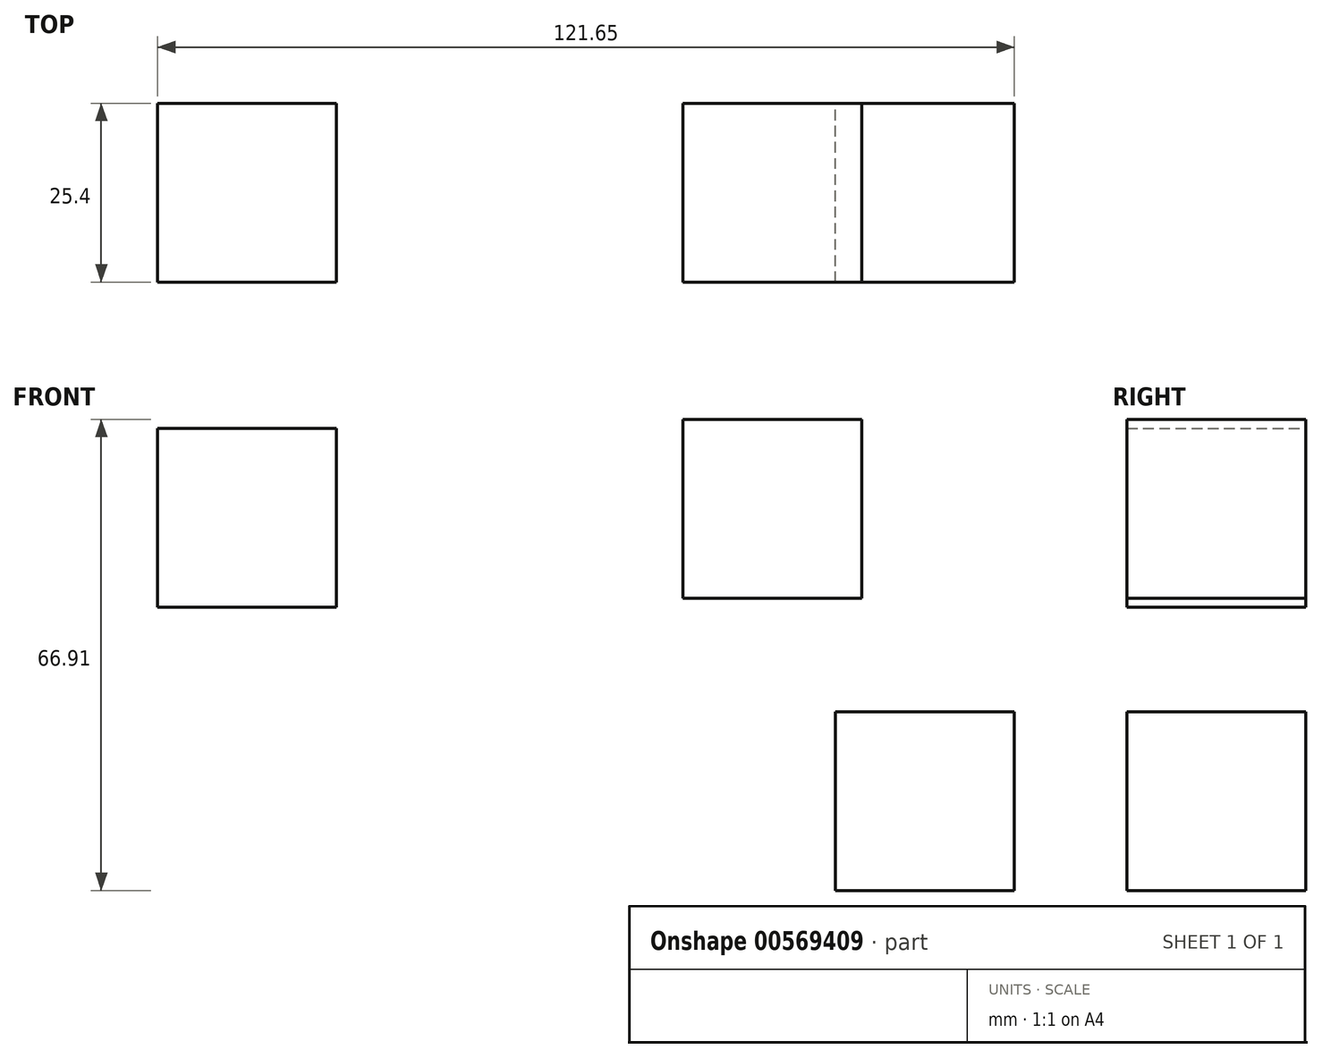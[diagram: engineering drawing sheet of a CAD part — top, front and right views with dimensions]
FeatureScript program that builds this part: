
annotation { "Feature Type Name" : "Feature", "Feature Type Description" : "" }
export const myFeature = defineFeature(function(context is Context, id is Id, definition is map)
    precondition{}
    {
        {
            var Q0;
            Q0=qCreatedBy(makeId("Front.planeOp"),FACE);
            var sketch = newSketch(context, id + "F0", { "sketchPlane" : qUnion([Q0])});
            skLineSegment(sketch, "E0.bottom", {"start": v(-67.13, 65.63) * mm, "end": v(-41.73, 65.63) * mm});
            skLineSegment(sketch, "E0.top", {"start": v(-67.13, 40.23) * mm, "end": v(-41.73, 40.23) * mm});
            skLineSegment(sketch, "E0.left", {"start": v(-67.13, 65.63) * mm, "end": v(-67.13, 40.23) * mm});
            skLineSegment(sketch, "E0.right", {"start": v(-41.73, 65.63) * mm, "end": v(-41.73, 40.23) * mm});
            skSolve(sketch);
        }
        {
            var Q0;
            Q0 = qSketchRegion(id + "F0", true);
            extrude(context, id + "F1", {"entities" : qUnion([Q0]), "depth" : 25.4 * mm, "offsetDistance" : 25.4 * mm});
        }
        {
            var Q0;
            Q0=qCreatedBy(makeId("Front.planeOp"),FACE);
            var sketch = newSketch(context, id + "F2", { "sketchPlane" : qUnion([Q0])});
            skLineSegment(sketch, "E1.bottom", {"start": v(7.48, 66.9) * mm, "end": v(32.88, 66.9) * mm});
            skLineSegment(sketch, "E1.top", {"start": v(7.48, 41.5) * mm, "end": v(32.88, 41.5) * mm});
            skLineSegment(sketch, "E1.left", {"start": v(7.48, 66.9) * mm, "end": v(7.48, 41.5) * mm});
            skLineSegment(sketch, "E1.right", {"start": v(32.88, 66.9) * mm, "end": v(32.88, 41.5) * mm});
            skSolve(sketch);
        }
        {
            var Q0;
            Q0 = qSketchRegion(id + "F2", true);
            extrude(context, id + "F3", {"entities" : qUnion([Q0]), "depth" : 25.4 * mm, "offsetDistance" : 25.4 * mm});
        }
        {
            var Q0;
            Q0=qCreatedBy(makeId("Front.planeOp"),FACE);
            var sketch = newSketch(context, id + "F4", { "sketchPlane" : qUnion([Q0])});
            skLineSegment(sketch, "E2.bottom", {"start": v(54.52, 25.4) * mm, "end": v(29.12, 25.4) * mm});
            skLineSegment(sketch, "E2.top", {"start": v(54.52, 0) * mm, "end": v(29.12, 0) * mm});
            skLineSegment(sketch, "E2.left", {"start": v(54.52, 25.4) * mm, "end": v(54.52, 0) * mm});
            skLineSegment(sketch, "E2.right", {"start": v(29.12, 25.4) * mm, "end": v(29.12, 0) * mm});
            skSolve(sketch);
        }
        {
            var Q0;
            Q0 = qSketchRegion(id + "F4", true);
            extrude(context, id + "F5", {"entities" : qUnion([Q0]), "depth" : 25.4 * mm, "offsetDistance" : 25.4 * mm});
        }
    });
